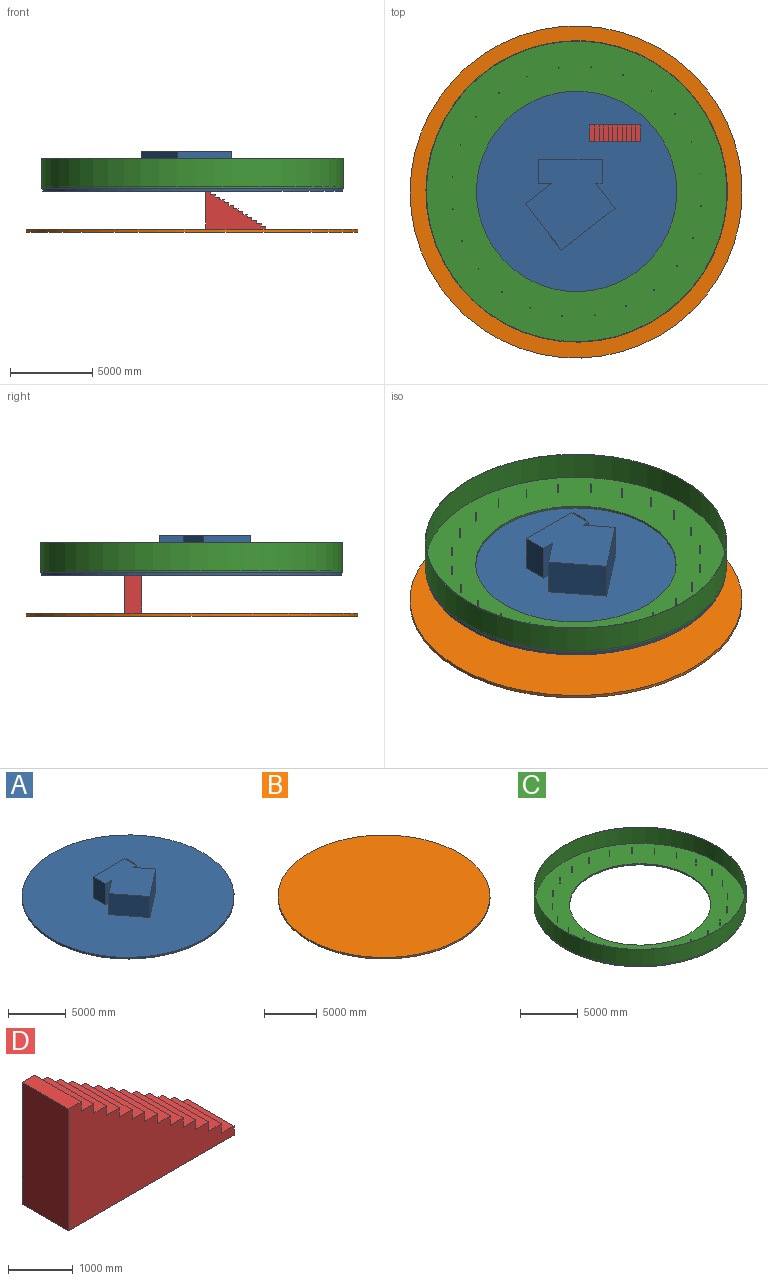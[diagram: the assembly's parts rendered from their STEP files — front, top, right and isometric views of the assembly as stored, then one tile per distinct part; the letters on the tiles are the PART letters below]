
ASSEMBLY  parts=4 mates=4
PART A: 17 faces, bbox 18288x18288x2387.6 mm
  f0: cylinder r=9144mm len=18288mm, axis (0,0,1), area 10215222.8mm2, adj f1,f2
  f1: plane 18288x18288mm, normal (0,0,-1), area 259580389.2mm2, adj f0,f3,f4,f5,f6
  f2: plane 18288x18288mm, normal (0,0,1), area 240880692.8mm2, adj f0,f3,f4,f5,f6,f7,f8,f9
  f3: plane 3048x177.8mm, normal (0,-1,0), area 541934.4mm2, adj f1,f2,f4,f5
  f4: plane 1016x177.8mm, normal (-1,0,0), area 180644.8mm2, adj f1,f2,f3,f6
  f5: plane 1016x177.8mm, normal (1,0,0), area 180644.8mm2, adj f1,f2,f3,f6
  f6: plane 3048x177.8mm, normal (0,1,0), area 541934.4mm2, adj f1,f2,f4,f5
  f7: plane 2209.8x1520.43mm, normal (0.79,0.61,0), area 4254886.1mm2, adj f2,f8,f15,f16
  f8: plane 2209.8x403.68mm, normal (0,-1,0), area 892044.6mm2, adj f2,f7,f9,f16
  f9: plane 2209.8x1465.16mm, normal (1,0,0), area 3237709.5mm2, adj f2,f8,f10,f16
  f10: plane 3872.61x2209.8mm, normal (0,1,0), area 8557683.8mm2, adj f2,f9,f11,f16
  f11: plane 2209.8x1465.16mm, normal (-1,0,0), area 3237709.5mm2, adj f2,f10,f12,f16
  f12: plane 2209.8x793.03mm, normal (0,-1,0), area 1752444.4mm2, adj f2,f11,f13,f16
  f13: plane 2209.8x1598.77mm, normal (-0.61,0.79,0), area 4474112mm2, adj f2,f12,f14,f16
  f14: plane 2816.9x2209.8mm, normal (-0.79,-0.61,0), area 7883013.1mm2, adj f2,f13,f15,f16
  f15: plane 3267.29x2538.73mm, normal (0.61,-0.79,0), area 9143433.9mm2, adj f2,f7,f14,f16
  f16: plane 5524.32x5456.06mm, normal (0,0,1), area 18699696.3mm2, adj f7,f8,f9,f10,f11,f12,f13,f14
PART B: 3 faces, bbox 20205.4x20205.4x177.8 mm
  f0: cylinder r=10102.71mm len=20205.43mm, axis (0,0,1), area 11286250.4mm2, adj f1,f2
  f1: plane 20205.43x20205.43mm, normal (0,0,-1), area 320646114.8mm2, adj f0
  f2: plane 20205.43x20205.43mm, normal (0,0,1), area 320646114.8mm2, adj f0
PART C: 54 faces, bbox 18338.8x18338.8x1828.8 mm
  f0: cylinder r=9144mm len=18288mm, axis (0,0,-1), area 97774275.2mm2, adj f2,f5
  f1: cylinder r=9169.4mm len=18338.8mm, axis (0,0,-1), area 105362726.4mm2, adj f2,f3
  f2: plane 18338.8x18338.8mm, normal (0,0,1), area 1461344.4mm2, adj f0,f1
  f3: plane 18338.8x18338.8mm, normal (0,0,-1), area 147393098.3mm2, adj f1,f4
  f4: cylinder r=6096mm len=12192mm, axis (0,0,-1), area 4864391.8mm2, adj f3,f5
  f5: plane 18288x18288mm, normal (0,0,1), area 145883110.1mm2, adj f0,f4,f6,f8,f10,f12,f14,f16
  f6: cylinder r=25.4mm len=609.6mm, axis (0,0,-1), area 97287.8mm2, adj f5,f7
  f7: plane 50.8x50.8mm, normal (0,0,1), area 2026.8mm2, adj f6
  f8: cylinder r=25.4mm len=609.6mm, axis (0,0,-1), area 97287.8mm2, adj f5,f9
  f9: plane 50.8x50.8mm, normal (0,0,1), area 2026.8mm2, adj f8
  f10: cylinder r=25.4mm len=609.6mm, axis (0,0,-1), area 97287.8mm2, adj f5,f11
  f11: plane 50.8x50.8mm, normal (0,0,1), area 2026.8mm2, adj f10
  f12: cylinder r=25.4mm len=609.6mm, axis (0,0,-1), area 97287.8mm2, adj f5,f13
  f13: plane 50.8x50.8mm, normal (0,0,1), area 2026.8mm2, adj f12
  f14: cylinder r=25.4mm len=609.6mm, axis (0,0,-1), area 97287.8mm2, adj f5,f15
  f15: plane 50.8x50.8mm, normal (0,0,1), area 2026.8mm2, adj f14
  f16: cylinder r=25.4mm len=609.6mm, axis (0,0,-1), area 97287.8mm2, adj f5,f17
  f17: plane 50.8x50.8mm, normal (0,0,1), area 2026.8mm2, adj f16
  f18: cylinder r=25.4mm len=609.6mm, axis (0,0,-1), area 97287.8mm2, adj f5,f19
  f19: plane 50.8x50.8mm, normal (0,0,1), area 2026.8mm2, adj f18
  f20: cylinder r=25.4mm len=609.6mm, axis (0,0,-1), area 97287.8mm2, adj f5,f21
  f21: plane 50.8x50.8mm, normal (0,0,1), area 2026.8mm2, adj f20
  f22: cylinder r=25.4mm len=609.6mm, axis (0,0,-1), area 97287.8mm2, adj f5,f23
  f23: plane 50.8x50.8mm, normal (0,0,1), area 2026.8mm2, adj f22
  f24: cylinder r=25.4mm len=609.6mm, axis (0,0,-1), area 97287.8mm2, adj f5,f25
  f25: plane 50.8x50.8mm, normal (0,0,1), area 2026.8mm2, adj f24
  f26: cylinder r=25.4mm len=609.6mm, axis (0,0,-1), area 97287.8mm2, adj f5,f27
  f27: plane 50.8x50.8mm, normal (0,0,1), area 2026.8mm2, adj f26
  f28: cylinder r=25.4mm len=609.6mm, axis (0,0,-1), area 97287.8mm2, adj f5,f29
  f29: plane 50.8x50.8mm, normal (0,0,1), area 2026.8mm2, adj f28
  f30: cylinder r=25.4mm len=609.6mm, axis (0,0,-1), area 97287.8mm2, adj f5,f31
  f31: plane 50.8x50.8mm, normal (0,0,1), area 2026.8mm2, adj f30
  f32: cylinder r=25.4mm len=609.6mm, axis (0,0,-1), area 97287.8mm2, adj f5,f33
  f33: plane 50.8x50.8mm, normal (0,0,1), area 2026.8mm2, adj f32
  f34: cylinder r=25.4mm len=609.6mm, axis (0,0,-1), area 97287.8mm2, adj f5,f35
  f35: plane 50.8x50.8mm, normal (0,0,1), area 2026.8mm2, adj f34
  f36: cylinder r=25.4mm len=609.6mm, axis (0,0,-1), area 97287.8mm2, adj f5,f37
  f37: plane 50.8x50.8mm, normal (0,0,1), area 2026.8mm2, adj f36
  f38: cylinder r=25.4mm len=609.6mm, axis (0,0,-1), area 97287.8mm2, adj f5,f39
  f39: plane 50.8x50.8mm, normal (0,0,1), area 2026.8mm2, adj f38
  f40: cylinder r=25.4mm len=609.6mm, axis (0,0,-1), area 97287.8mm2, adj f5,f41
  f41: plane 50.8x50.8mm, normal (0,0,1), area 2026.8mm2, adj f40
  f42: cylinder r=25.4mm len=609.6mm, axis (0,0,-1), area 97287.8mm2, adj f5,f43
  f43: plane 50.8x50.8mm, normal (0,0,1), area 2026.8mm2, adj f42
  f44: cylinder r=25.4mm len=609.6mm, axis (0,0,-1), area 97287.8mm2, adj f5,f45
  f45: plane 50.8x50.8mm, normal (0,0,1), area 2026.8mm2, adj f44
  f46: cylinder r=25.4mm len=609.6mm, axis (0,0,-1), area 97287.8mm2, adj f5,f47
  f47: plane 50.8x50.8mm, normal (0,0,1), area 2026.8mm2, adj f46
  f48: cylinder r=25.4mm len=609.6mm, axis (0,0,-1), area 97287.8mm2, adj f5,f49
  f49: plane 50.8x50.8mm, normal (0,0,1), area 2026.8mm2, adj f48
  f50: cylinder r=25.4mm len=609.6mm, axis (0,0,-1), area 97287.8mm2, adj f5,f51
  f51: plane 50.8x50.8mm, normal (0,0,1), area 2026.8mm2, adj f50
  f52: cylinder r=25.4mm len=609.6mm, axis (0,0,-1), area 97287.8mm2, adj f5,f53
  f53: plane 50.8x50.8mm, normal (0,0,1), area 2026.8mm2, adj f52
PART D: 30 faces, bbox 3632.2x1016x2311.4 mm
  f0: plane 3632.2x2311.4mm, normal (0,1,0), area 4520636.1mm2, adj f1,f2,f3,f4,f5,f6,f7,f8
  f1: plane 2311.4x1016mm, normal (-1,0,0), area 2348382.4mm2, adj f0,f2,f28,f29
  f2: plane 1016x279.4mm, normal (0,0,1), area 283870.4mm2, adj f0,f1,f3,f29
  f3: plane 1016x177.8mm, normal (1,0,0), area 180644.8mm2, adj f0,f2,f4,f29
  f4: plane 1016x279.4mm, normal (0,0,1), area 283870.4mm2, adj f0,f3,f5,f29
  f5: plane 1016x177.8mm, normal (1,0,0), area 180644.8mm2, adj f0,f4,f6,f29
  f6: plane 1016x279.4mm, normal (0,0,1), area 283870.4mm2, adj f0,f5,f7,f29
  f7: plane 1016x177.8mm, normal (1,0,0), area 180644.8mm2, adj f0,f6,f8,f29
  f8: plane 1016x279.4mm, normal (0,0,1), area 283870.4mm2, adj f0,f7,f9,f29
  f9: plane 1016x177.8mm, normal (1,0,0), area 180644.8mm2, adj f0,f8,f10,f29
  f10: plane 1016x279.4mm, normal (0,0,1), area 283870.4mm2, adj f0,f9,f11,f29
  f11: plane 1016x177.8mm, normal (1,0,0), area 180644.8mm2, adj f0,f10,f12,f29
  f12: plane 1016x279.4mm, normal (0,0,1), area 283870.4mm2, adj f0,f11,f13,f29
  f13: plane 1016x177.8mm, normal (1,0,0), area 180644.8mm2, adj f0,f12,f14,f29
  f14: plane 1016x279.4mm, normal (0,0,1), area 283870.4mm2, adj f0,f13,f15,f29
  f15: plane 1016x177.8mm, normal (1,0,0), area 180644.8mm2, adj f0,f14,f16,f29
  f16: plane 1016x279.4mm, normal (0,0,1), area 283870.4mm2, adj f0,f15,f17,f29
  f17: plane 1016x177.8mm, normal (1,0,0), area 180644.8mm2, adj f0,f16,f18,f29
  f18: plane 1016x279.4mm, normal (0,0,1), area 283870.4mm2, adj f0,f17,f19,f29
  f19: plane 1016x177.8mm, normal (1,0,0), area 180644.8mm2, adj f0,f18,f20,f29
  f20: plane 1016x279.4mm, normal (0,0,1), area 283870.4mm2, adj f0,f19,f21,f29
  f21: plane 1016x177.8mm, normal (1,0,0), area 180644.8mm2, adj f0,f20,f22,f29
  f22: plane 1016x279.4mm, normal (0,0,1), area 283870.4mm2, adj f0,f21,f23,f29
  f23: plane 1016x177.8mm, normal (1,0,0), area 180644.8mm2, adj f0,f22,f24,f29
  f24: plane 1016x279.4mm, normal (0,0,1), area 283870.4mm2, adj f0,f23,f25,f29
  f25: plane 1016x177.8mm, normal (1,0,0), area 180644.8mm2, adj f0,f24,f26,f29
  f26: plane 1016x279.4mm, normal (0,0,1), area 283870.4mm2, adj f0,f25,f27,f29
  f27: plane 1016x177.8mm, normal (1,0,0), area 180644.8mm2, adj f0,f26,f28,f29
  f28: plane 3632.2x1016mm, normal (0,0,-1), area 3690315.2mm2, adj f0,f1,f27,f29
  f29: plane 3632.2x2311.4mm, normal (0,-1,0), area 4520636.1mm2, adj f1,f2,f3,f4,f5,f6,f7,f8
PLACE A rot(axis=(-1,0,0),0deg) t=(27.88,42.08,2489.2)mm
PLACE B rot(axis=(-1,0,0),0deg) t=(0,0,2489.2)mm
PLACE C rot(axis=(0,0,1),2.8deg) t=(30.18,30.08,2489.2)mm
PLACE D rot(axis=(-1,0,0),0deg) t=(27.88,42.08,2489.2)mm
MATE revolute C.f4 <-> A.f2  axis (0,0,-1) through (30.18,30.08,2489.2)mm
MATE slider B.f0 <-> A.f1  axis (0,0,1) through (0,0,0)mm
MATE fastened D.f2 <-> A.f1  axis (0,0,1) through (841.13,3569.75,2311.4)mm
MATE planar D.f28 <-> B.f0  axis (0,0,-1) through (2657.23,3569.75,0)mm
